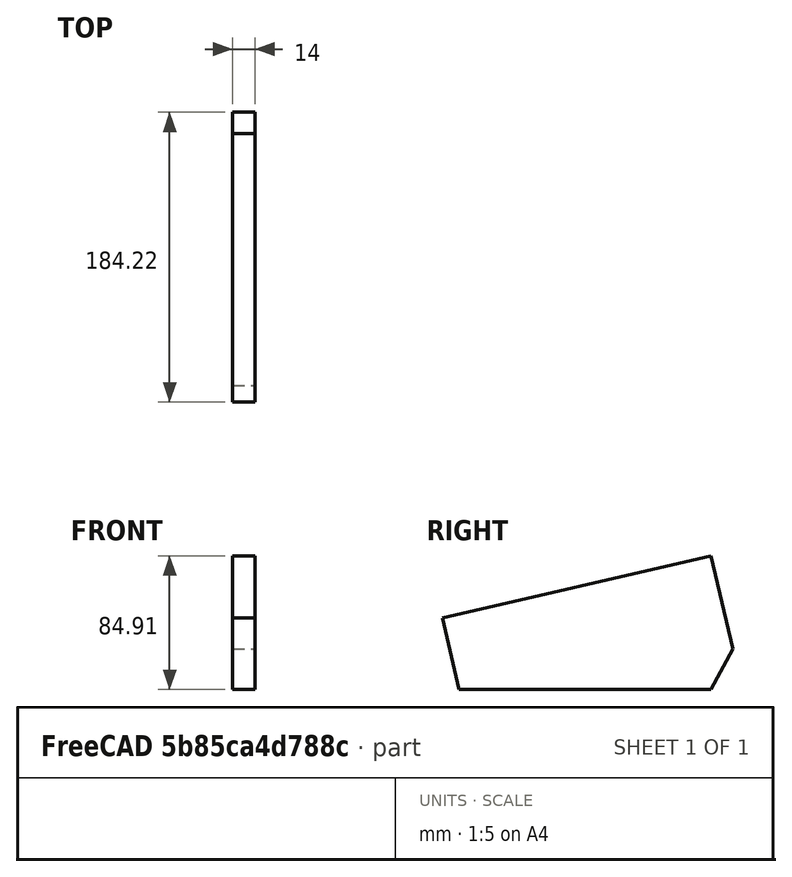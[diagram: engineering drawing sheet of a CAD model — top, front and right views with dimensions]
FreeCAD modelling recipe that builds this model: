
FCSTD DOCUMENT  (FreeCAD 1.0R39109 (Git))
Label: Griffschale Zeichnung
License: All rights reserved
objects: TechDraw::DrawViewDimension×13, TechDraw::DrawProjGroupItem×2, Sketcher::SketchObject×1, PartDesign::Pad×1, PartDesign::Body×1, TechDraw::DrawSVGTemplate×1, TechDraw::DrawProjGroup×1, TechDraw::DrawPage×1
note: 27 computed .brp shape members not serialized (recipe doc carries the construction recipe); baked Part::Feature solids carry a one-line shape summary decoded from their .brp

FEATURE [Sketcher::SketchObject] Sketch
  ArcFitTolerance = 1e-06
  AttachmentSupport = -> [YZ_Plane]
  FullyConstrained = false
  MakeInternals = false
  MapMode = 5
  Placement = pos=(0,0,0) rot=(0.57735,0.57735,0.57735;2.0944rad)
  sketch-geometry (9):
    g0: LineSegment StartX=-3.97348 StartY=-71.0601 StartZ=0 EndX=156.027 EndY=-71.0601 EndZ=0
    g1: LineSegment StartX=156.027 StartY=-71.0601 StartZ=0 EndX=169.729 EndY=-45.5015 EndZ=0
    g2: LineSegment StartX=169.729 StartY=-45.5015 StartZ=0 EndX=156.027 EndY=13.8508 EndZ=0
    g3: LineSegment StartX=156.027 StartY=13.8508 StartZ=0 EndX=-14.4882 EndY=-25.5156 EndZ=0
    g4: LineSegment StartX=-14.4882 StartY=-25.5156 StartZ=0 EndX=-3.97348 EndY=-71.0601 EndZ=0
    g5: LineSegment [constr] StartX=156.027 StartY=13.8508 StartZ=0 EndX=-211.763 EndY=-71.0601 EndZ=0
    g6: LineSegment [constr] StartX=156.027 StartY=-71.0601 StartZ=0 EndX=-211.763 EndY=-71.0601 EndZ=0
    g7: LineSegment [constr] StartX=156.027 StartY=13.8508 StartZ=0 EndX=156.027 EndY=-71.0601 EndZ=0
    g8: LineSegment [constr] StartX=-14.4882 StartY=-25.5156 StartZ=0 EndX=-14.4882 EndY=-71.0601 EndZ=0
  constraints (23):
    c: Coincident(g0,g1)
    c: Coincident(g1,g2)
    c: Coincident(g2,g3)
    c: Coincident(g3,g4)
    c: Coincident(g4,g0)
    c: Coincident(g5,g2)
    c: Coincident(g6,g0)
    c: Horizontal(g6)
    c: Coincident(g5,g6)
    c: Angle(g6,g5) = 0.226893
    c: Distance(g3) = 175
    c: DistanceX(g0,g0) = 160
    c: Coincident(g7,g2)
    c: Coincident(g7,g0)
    c: Vertical(g7)
    c: Angle(g3,g2) = 1.5708
    c: Angle(g4,g3) = 1.5708
    c: PointOnObject(g3,g5)
    c: PointOnObject(g0,g6)
    c: Coincident(g8,g3)
    c: PointOnObject(g8,g6)
    c: Vertical(g8)
    c: Distance(g1) = 29
FEATURE [PartDesign::Pad] Pad
  Direction = (1,0,0)
  Length = 14
  Length2 = 10
  Placement = pos=(0,0,0) rot=(1,1,1;2.0944rad)
  Profile = -> Sketch
  ReferenceAxis = -> Sketch [N_Axis]
  Refine = true
  Suppressed = false
  Type = 0
FEATURE [PartDesign::Body] Body  label="Körper"
  AllowCompound = false
  Group = -> [Sketch,Pad]
  Origin = -> Origin
  Tip = -> Pad
FEATURE [TechDraw::DrawSVGTemplate] Template  label="Vorlage"
  EditableTexts = approval_person=B. Hecate; creator=Andreas Schumm; date_of_issue=17.02.2025; document_type=Assembly Drawing; general_tolerances=ISO 2768-m; identification_number=DN; language_code=EN; legal_owner_1=crazy-midi.de; part_material=Holz; revision_index=AAA; sheet_number=1 / 1; sheet_scale=1 : 1; title=Griffschale
  Height = 210
  Orientation = 1
  Template = C:/Program Files/FreeCAD 1.0/data/Mod/TechDraw/Templates/A4_Landscape_ISO5457_minimal.svg
  Width = 297
FEATURE [TechDraw::DrawProjGroupItem] View  label="Front"
  CoarseView = false
  Direction = (0,0,1)
  Focus = 100
  HardHidden = false
  IsoCount = 0
  IsoHidden = false
  IsoVisible = false
  LockPosition = true
  Perspective = false
  Rotation = 0
  RotationVector = (1,0,0)
  ScaleType = 2
  ScrubCount = 1
  SeamHidden = false
  SeamVisible = false
  SmoothHidden = false
  SmoothVisible = true
  Source = -> [Body]
  Type = 0
  X = 0
  XDirection = (1e-16,-1,0)
  Y = 0
FEATURE [TechDraw::DrawViewDimension] Dimension010  label="Maß010"
  AngleOverride = false
  Arbitrary = false
  ArbitraryTolerances = false
  BoxCorners = (2) [(-92.1087,-7,0),(92.1087,7,0)]
  EqualTolerance = true
  ExtensionAngle = 0
  FormatSpec = %.2w
  FormatSpecOverTolerance = %+.2w
  FormatSpecUnderTolerance = %+.2w
  Inverted = false
  LineAngle = 0
  LockPosition = false
  MeasureType = 1
  OverTolerance = 0
  References2D = -> [View]
  Rotation = 0
  ScaleType = 0
  TheoreticalExact = false
  Type = 0
  UnderTolerance = 0
  X = -106.826
  Y = 0
FEATURE [TechDraw::DrawProjGroupItem] ProjItem  label="Untersicht"
  CoarseView = false
  Direction = (-1,-1e-16,0)
  Focus = 100
  HardHidden = false
  IsoCount = 0
  IsoHidden = false
  IsoVisible = false
  LockPosition = false
  Perspective = false
  Rotation = 0
  RotationVector = (1,0,0)
  ScaleType = 0
  ScrubCount = 1
  SeamHidden = false
  SeamVisible = false
  SmoothHidden = false
  SmoothVisible = true
  Source = -> [Body]
  Type = 5
  X = 0
  XDirection = (1e-16,-1,0)
  Y = 64.4554
FEATURE [TechDraw::DrawProjGroup] ProjGroup
  Anchor = -> View
  AutoDistribute = true
  LockPosition = false
  ProjectionType = 0
  Rotation = 0
  ScaleType = 0
  Source = -> [Body]
  Views = -> [View,ProjItem]
  X = 154.736
  Y = 83.2975
  spacingX = 15
  spacingY = 15
FEATURE [TechDraw::DrawViewDimension] Dimension  label="Maß"
  AngleOverride = false
  Arbitrary = false
  ArbitraryTolerances = false
  BoxCorners = (2) [(-92.1087,-42.4554,0),(92.1087,42.4554,0)]
  EqualTolerance = true
  ExtensionAngle = 0
  FormatSpec = %.2w
  FormatSpecOverTolerance = %+.2w
  FormatSpecUnderTolerance = %+.2w
  Inverted = false
  LineAngle = 0
  LockPosition = false
  MeasureType = 1
  OverTolerance = 0
  References2D = -> [ProjItem]
  Rotation = 0
  ScaleType = 0
  TheoreticalExact = false
  Type = 0
  UnderTolerance = 0
  X = 8.98946
  Y = 32.0337
FEATURE [TechDraw::DrawViewDimension] Dimension008  label="Maß008"
  AngleOverride = false
  Arbitrary = false
  ArbitraryTolerances = false
  BoxCorners = (2) [(-92.1087,-42.4554,0),(92.1087,42.4554,0)]
  EqualTolerance = true
  ExtensionAngle = 0
  FormatSpec = %.2w
  FormatSpecOverTolerance = %+.2w
  FormatSpecUnderTolerance = %+.2w
  Inverted = false
  LineAngle = 0
  LockPosition = false
  MeasureType = 1
  OverTolerance = 0
  References2D = -> [ProjItem]
  Rotation = 0
  ScaleType = 0
  TheoreticalExact = false
  Type = 6
  UnderTolerance = 0
  X = -59.9984
  Y = -31.8576
FEATURE [TechDraw::DrawViewDimension] Dimension004  label="Maß004"
  AngleOverride = false
  Arbitrary = false
  ArbitraryTolerances = false
  BoxCorners = (2) [(-92.1087,-42.4554,0),(92.1087,42.4554,0)]
  EqualTolerance = true
  ExtensionAngle = 0
  FormatSpec = %.2w
  FormatSpecOverTolerance = %+.2w
  FormatSpecUnderTolerance = %+.2w
  Inverted = false
  LineAngle = 0
  LockPosition = false
  MeasureType = 1
  OverTolerance = 0
  References2D = -> [ProjItem]
  Rotation = 0
  ScaleType = 0
  TheoreticalExact = false
  Type = 0
  UnderTolerance = 0
  X = -100.517
  Y = 16.3022
FEATURE [TechDraw::DrawViewDimension] Dimension003  label="Maß003"
  AngleOverride = false
  Arbitrary = false
  ArbitraryTolerances = false
  BoxCorners = (2) [(-92.1087,-42.4554,0),(92.1087,42.4554,0)]
  EqualTolerance = true
  ExtensionAngle = 0
  FormatSpec = %.2w
  FormatSpecOverTolerance = %+.2w
  FormatSpecUnderTolerance = %+.2w
  Inverted = false
  LineAngle = 0
  LockPosition = false
  MeasureType = 1
  OverTolerance = 0
  References2D = -> [ProjItem]
  Rotation = 0
  ScaleType = 0
  TheoreticalExact = false
  Type = 0
  UnderTolerance = 0
  X = -89.6813
  Y = -32.0479
FEATURE [TechDraw::DrawViewDimension] Dimension007  label="Maß007"
  AngleOverride = false
  Arbitrary = false
  ArbitraryTolerances = false
  BoxCorners = (2) [(-92.1087,-42.4554,0),(92.1087,42.4554,0)]
  EqualTolerance = true
  ExtensionAngle = 0
  FormatSpec = %.2w
  FormatSpecOverTolerance = %+.2w
  FormatSpecUnderTolerance = %+.2w
  Inverted = false
  LineAngle = 0
  LockPosition = false
  MeasureType = 1
  OverTolerance = 0
  References2D = -> [ProjItem]
  Rotation = 0
  ScaleType = 0
  TheoreticalExact = false
  Type = 0
  UnderTolerance = 0
  X = -3.26825
  Y = -47.4074
FEATURE [TechDraw::DrawViewDimension] Dimension005  label="Maß005"
  AngleOverride = false
  Arbitrary = false
  ArbitraryTolerances = false
  BoxCorners = (2) [(-92.1087,-42.4554,0),(92.1087,42.4554,0)]
  EqualTolerance = true
  ExtensionAngle = 0
  FormatSpec = %.2w
  FormatSpecOverTolerance = %+.2w
  FormatSpecUnderTolerance = %+.2w
  Inverted = false
  LineAngle = 0
  LockPosition = false
  MeasureType = 1
  OverTolerance = 0
  References2D = -> [ProjItem]
  Rotation = 0
  ScaleType = 0
  TheoreticalExact = false
  Type = 0
  UnderTolerance = 0
  X = 102.788
  Y = -19.6343
FEATURE [TechDraw::DrawViewDimension] Dimension006  label="Maß006"
  AngleOverride = false
  Arbitrary = false
  ArbitraryTolerances = false
  BoxCorners = (2) [(-92.1087,-42.4554,0),(92.1087,42.4554,0)]
  EqualTolerance = true
  ExtensionAngle = 0
  FormatSpec = %.2w
  FormatSpecOverTolerance = %+.2w
  FormatSpecUnderTolerance = %+.2w
  Inverted = false
  LineAngle = 0
  LockPosition = false
  MeasureType = 1
  OverTolerance = 0
  References2D = -> [ProjItem]
  Rotation = 0
  ScaleType = 0
  TheoreticalExact = false
  Type = 6
  UnderTolerance = 0
  X = 64.9156
  Y = -9.62233
FEATURE [TechDraw::DrawViewDimension] Dimension009  label="Maß009"
  AngleOverride = false
  Arbitrary = false
  ArbitraryTolerances = false
  BoxCorners = (2) [(-92.1087,-42.4554,0),(92.1087,42.4554,0)]
  EqualTolerance = true
  ExtensionAngle = 0
  FormatSpec = %.2w
  FormatSpecOverTolerance = %+.2w
  FormatSpecUnderTolerance = %+.2w
  Inverted = false
  LineAngle = 0
  LockPosition = false
  MeasureType = 1
  OverTolerance = 0
  References2D = -> [ProjItem]
  Rotation = 0
  ScaleType = 0
  TheoreticalExact = false
  Type = 6
  UnderTolerance = 0
  X = -77.2108
  Y = -15.8925
FEATURE [TechDraw::DrawViewDimension] Dimension011  label="Maß011"
  AngleOverride = false
  Arbitrary = false
  ArbitraryTolerances = false
  BoxCorners = (2) [(-92.1087,-42.4554,0),(92.1087,42.4554,0)]
  EqualTolerance = true
  ExtensionAngle = 0
  FormatSpec = %.2w
  FormatSpecOverTolerance = %+.2w
  FormatSpecUnderTolerance = %+.2w
  Inverted = false
  LineAngle = 0
  LockPosition = false
  MeasureType = 1
  OverTolerance = 0
  References2D = -> [ProjItem]
  Rotation = 0
  ScaleType = 0
  TheoreticalExact = false
  Type = 2
  UnderTolerance = 0
  X = -123.308
  Y = 0
FEATURE [TechDraw::DrawViewDimension] Dimension013  label="Maß013"
  AngleOverride = false
  Arbitrary = false
  ArbitraryTolerances = false
  BoxCorners = (2) [(-92.1087,-7,0),(92.1087,7,0)]
  EqualTolerance = true
  ExtensionAngle = 0
  FormatSpec = %.2w
  FormatSpecOverTolerance = %+.2w
  FormatSpecUnderTolerance = %+.2w
  Inverted = false
  LineAngle = 0
  LockPosition = false
  MeasureType = 1
  OverTolerance = 0
  References2D = -> [View]
  Rotation = 0
  ScaleType = 0
  TheoreticalExact = false
  Type = 1
  UnderTolerance = 0
  X = 0
  Y = -11.9734
FEATURE [TechDraw::DrawViewDimension] Dimension014  label="Maß014"
  AngleOverride = false
  Arbitrary = false
  ArbitraryTolerances = false
  BoxCorners = (2) [(-92.1087,-42.4554,0),(92.1087,42.4554,0)]
  EqualTolerance = true
  ExtensionAngle = 0
  FormatSpec = %.2w
  FormatSpecOverTolerance = %+.2w
  FormatSpecUnderTolerance = %+.2w
  Inverted = false
  LineAngle = 0
  LockPosition = false
  MeasureType = 1
  OverTolerance = 0
  References2D = -> [ProjItem]
  Rotation = 0
  ScaleType = 0
  TheoreticalExact = false
  Type = 2
  UnderTolerance = 0
  X = 119.263
  Y = -13.0782
FEATURE [TechDraw::DrawViewDimension] Dimension015  label="Maß015"
  AngleOverride = false
  Arbitrary = false
  ArbitraryTolerances = false
  BoxCorners = (2) [(-92.1087,-42.4554,0),(92.1087,42.4554,0)]
  EqualTolerance = true
  ExtensionAngle = 0
  FormatSpec = %.2w
  FormatSpecOverTolerance = %+.2w
  FormatSpecUnderTolerance = %+.2w
  Inverted = false
  LineAngle = 0
  LockPosition = false
  MeasureType = 1
  OverTolerance = 0
  References2D = -> [ProjItem]
  Rotation = 0
  ScaleType = 0
  TheoreticalExact = false
  Type = 2
  UnderTolerance = 0
  X = -113.636
  Y = -29.68
FEATURE [TechDraw::DrawPage] Page  label="Seite"
  KeepUpdated = true
  NextBalloonIndex = 1
  ProjectionType = 0
  Template = -> Template
  Views = -> [ProjGroup,Dimension,Dimension003,Dimension004,Dimension005,Dimension006,Dimension007,Dimension008,Dimension009,Dimension010,Dimension011,Dimension013,Dimension014,Dimension015]
